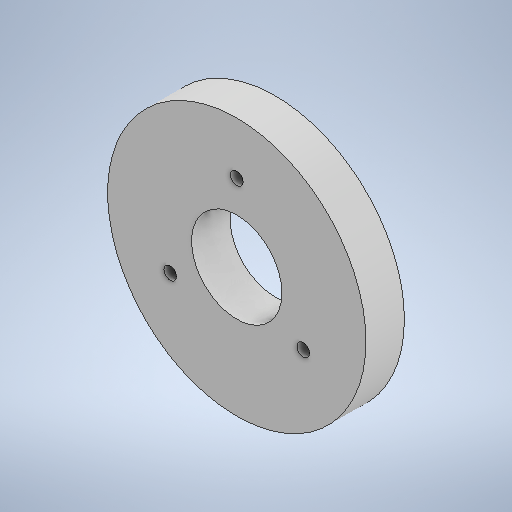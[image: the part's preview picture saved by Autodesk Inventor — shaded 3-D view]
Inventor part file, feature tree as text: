
AUTODESK INVENTOR PART (.ipt)
format: ipt  version: 2025 (Build 290162000, 162)  size: 223,744 bytes
history: native  units: mm
features: sketch x2, extrude x1
ambient origin geometry x8: Origin, YZ Plane, XZ Plane, XY Plane, X Axis, Y Axis, Z Axis, Center Point
bodies: 实体1 (feature_tree)
feature tree (3):
  extrude  "拉伸1"  Depth=40.0mm
  sketch  "草图1"  dims[d0=67.2mm d1=40.0mm]
  sketch  "草图 - 环形阵列1"  dims[d2=3.3mm d3=30.0mm d5=360.0deg d7=23.5mm d8=10.0mm d9=0.0mm]
